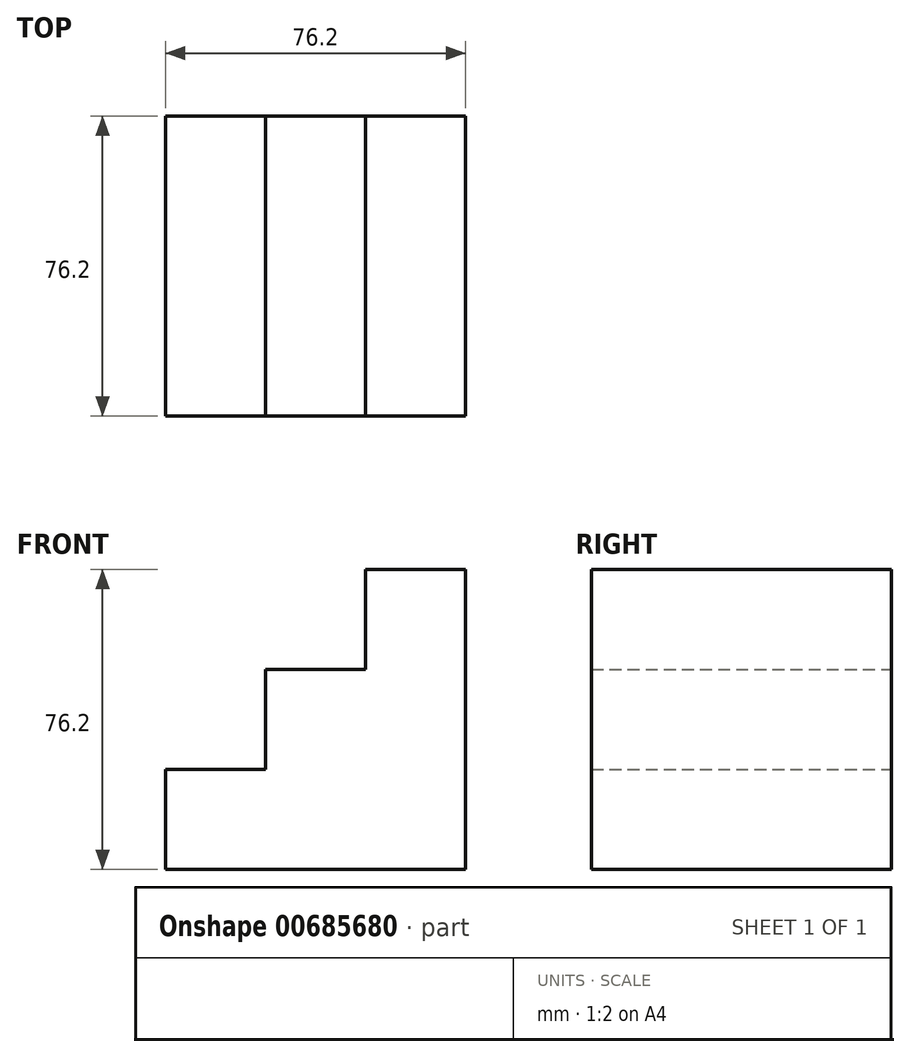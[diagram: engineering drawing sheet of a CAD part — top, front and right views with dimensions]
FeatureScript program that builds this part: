
annotation { "Feature Type Name" : "Feature", "Feature Type Description" : "" }
export const myFeature = defineFeature(function(context is Context, id is Id, definition is map)
    precondition{}
    {
        {
            var Q0;
            Q0=qCreatedBy(makeId("Front.planeOp"),FACE);
            var sketch = newSketch(context, id + "F0", { "sketchPlane" : qUnion([Q0])});
            skLineSegment(sketch, "E0", {"start": v(-41.88, -21.65) * mm, "end": v(-41.88, 3.75) * mm});
            skLineSegment(sketch, "E1", {"start": v(-41.88, 3.75) * mm, "end": v(-16.48, 3.75) * mm});
            skLineSegment(sketch, "E2", {"start": v(-16.48, 3.75) * mm, "end": v(-16.48, 29.15) * mm});
            skLineSegment(sketch, "E3", {"start": v(-16.48, 29.15) * mm, "end": v(8.92, 29.15) * mm});
            skLineSegment(sketch, "E4", {"start": v(8.92, 29.15) * mm, "end": v(8.92, 54.55) * mm});
            skLineSegment(sketch, "E5", {"start": v(8.92, 54.55) * mm, "end": v(34.32, 54.55) * mm});
            skLineSegment(sketch, "E6", {"start": v(34.32, 54.55) * mm, "end": v(34.32, -21.65) * mm});
            skLineSegment(sketch, "E7", {"start": v(34.32, -21.65) * mm, "end": v(-41.88, -21.65) * mm});
            skSolve(sketch);
        }
        {
            var Q0;
            Q0 = qSketchRegion(id + "F0", true);
            extrude(context, id + "F1", {"entities" : qUnion([Q0]), "depth" : 76.2 * mm, "offsetDistance" : 25.4 * mm});
        }
    });
